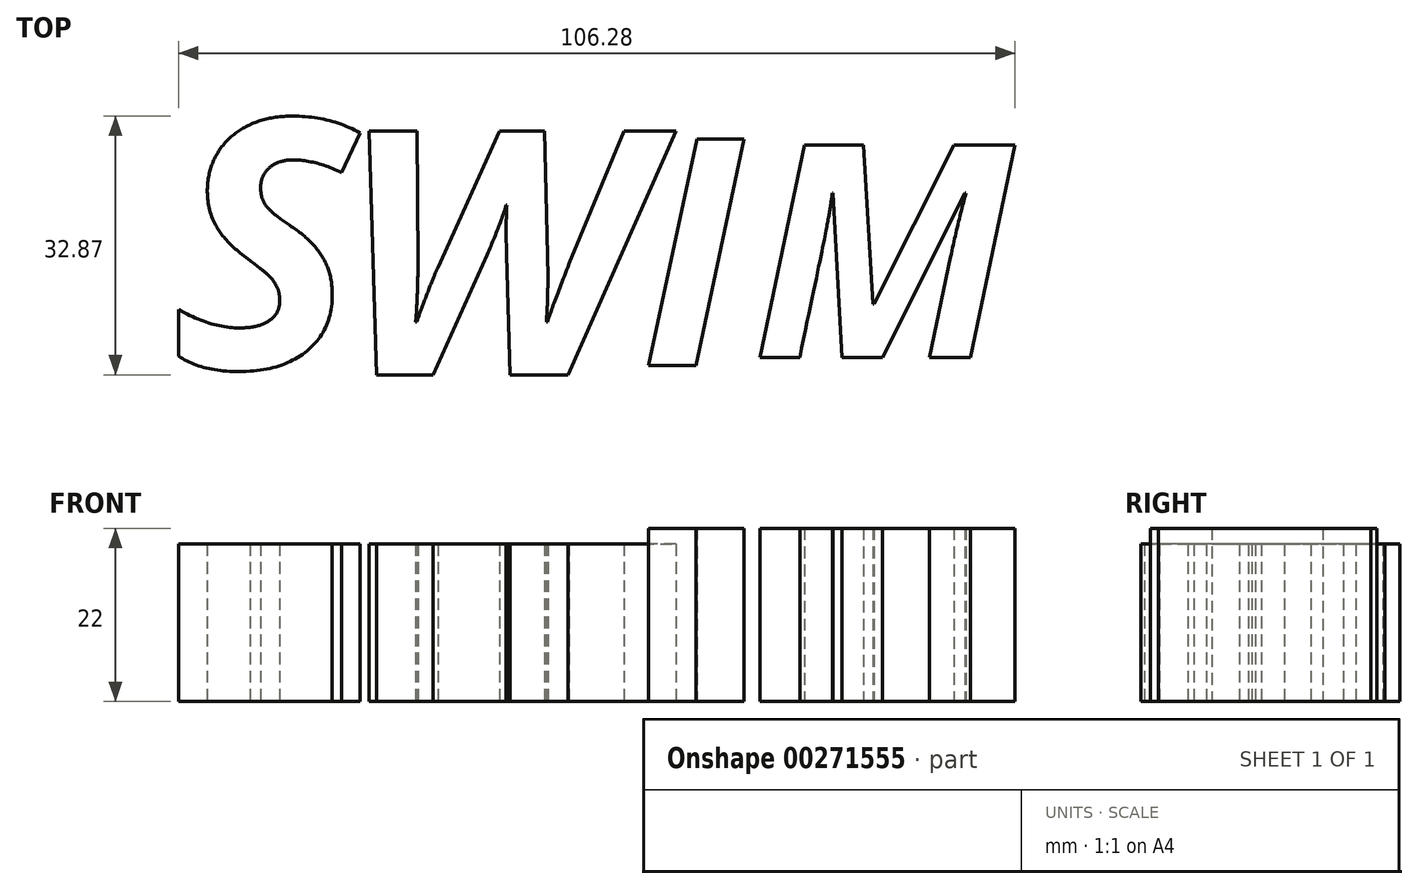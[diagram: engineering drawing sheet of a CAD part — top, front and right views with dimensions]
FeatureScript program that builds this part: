
annotation { "Feature Type Name" : "Feature", "Feature Type Description" : "" }
export const myFeature = defineFeature(function(context is Context, id is Id, definition is map)
    precondition{}
    {
        {
            var Q0;
            Q0=qCreatedBy(makeId("Top.planeOp"),FACE);
            var sketch = newSketch(context, id + "F0", { "sketchPlane" : qUnion([Q0])});
            skText(sketch, "E0", { "text": "S", "fontName": "OpenSans-BoldItalic.ttf"});
            const initialGuessF0  = {"E0": [-0.06686, -0.01567, 1, 0, 0.03184]};
            skSetInitialGuess(sketch, initialGuessF0);
            skSolve(sketch);
        }
        {
            var Q0;
            Q0 = qSketchRegion(id + "F0", true);
            extrude(context, id + "F1", {"entities" : qUnion([Q0]), "depth" : 20 * mm});
        }
        {
            var Q0;
            Q0=qCreatedBy(makeId("Top.planeOp"),FACE);
            var sketch = newSketch(context, id + "F2", { "sketchPlane" : qUnion([Q0])});
            skText(sketch, "E1", { "text": "W", "fontName": "OpenSans-BoldItalic.ttf"});
            const initialGuessF2  = {"E1": [-0.04565, -0.01652, 1, 0, 0.03123]};
            skSetInitialGuess(sketch, initialGuessF2);
            skSolve(sketch);
        }
        {
            var Q0;
            Q0 = qSketchRegion(id + "F2", true);
            extrude(context, id + "F3", {"entities" : qUnion([Q0]), "depth" : 20 * mm});
        }
        {
            var Q0;
            Q0=qCreatedBy(makeId("Top.planeOp"),FACE);
            var sketch = newSketch(context, id + "F4", { "sketchPlane" : qUnion([Q0])});
            skText(sketch, "E2", { "text": "I", "fontName": "OpenSans-BoldItalic.ttf"});
            const initialGuessF4  = {"E2": [-0.0073, -0.01531, 1, 0, 0.029]};
            skSetInitialGuess(sketch, initialGuessF4);
            skSolve(sketch);
        }
        {
            var Q0;
            Q0 = qSketchRegion(id + "F4", true);
            extrude(context, id + "F5", {"entities" : qUnion([Q0]), "depth" : 22 * mm});
        }
        {
            var Q0;
            Q0=qCreatedBy(makeId("Top.planeOp"),FACE);
            var sketch = newSketch(context, id + "F6", { "sketchPlane" : qUnion([Q0])});
            skText(sketch, "E3", { "text": "M", "fontName": "OpenSans-BoldItalic.ttf"});
            const initialGuessF6  = {"E3": [0.0069, -0.0143, 1, 0, 0.02718]};
            skSetInitialGuess(sketch, initialGuessF6);
            skSolve(sketch);
        }
        {
            var Q0;
            Q0 = qSketchRegion(id + "F6", true);
            extrude(context, id + "F7", {"entities" : qUnion([Q0]), "depth" : 22 * mm});
        }
    });
